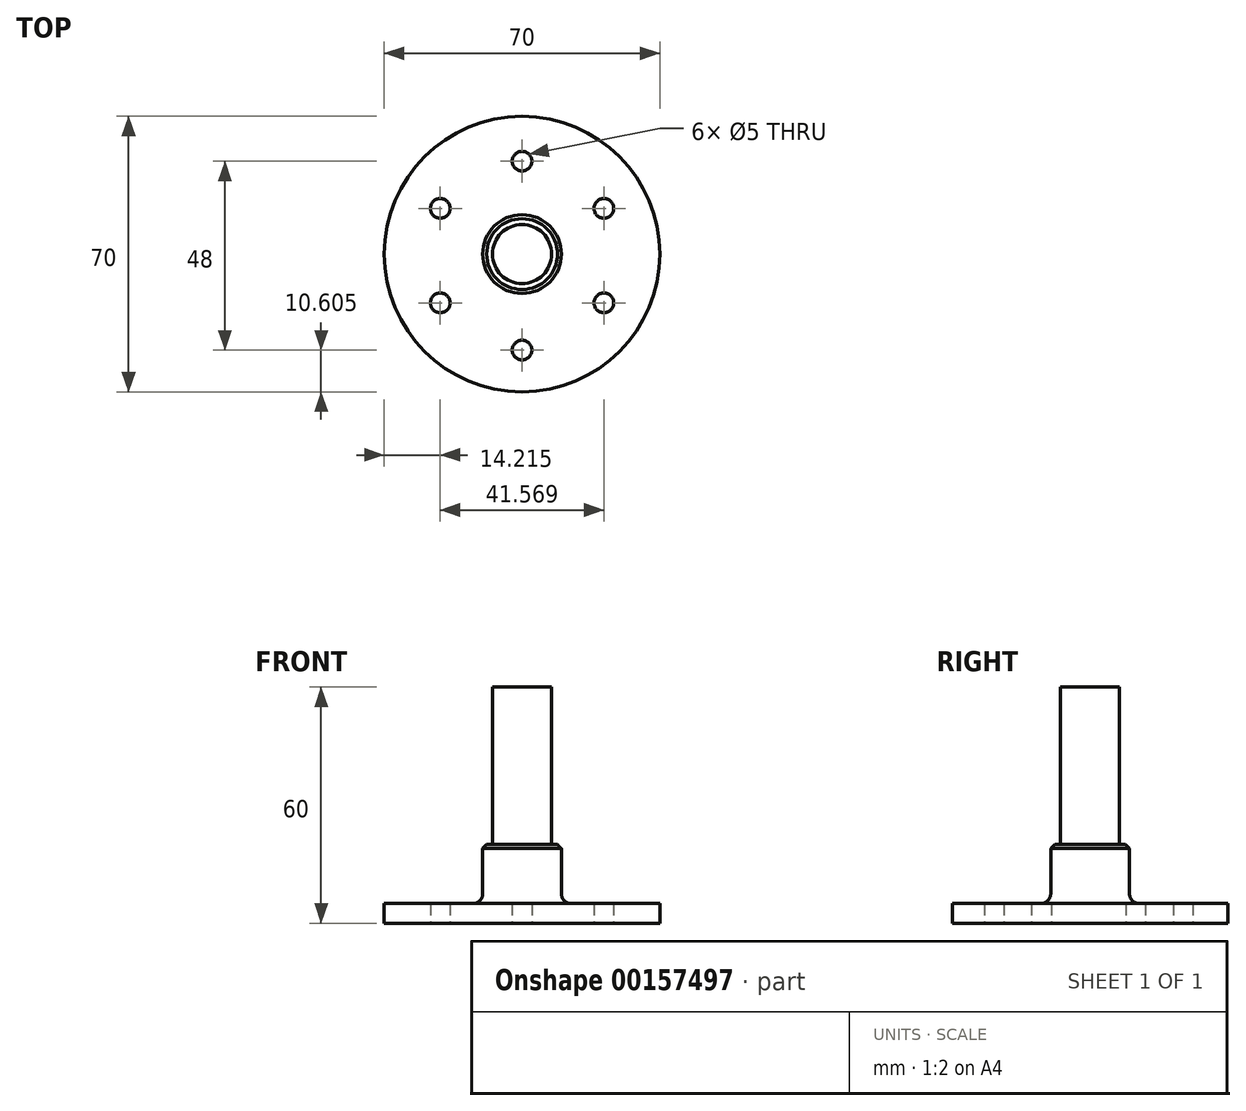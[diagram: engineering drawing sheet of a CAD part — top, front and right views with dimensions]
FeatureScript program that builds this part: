
annotation { "Feature Type Name" : "Feature", "Feature Type Description" : "" }
export const myFeature = defineFeature(function(context is Context, id is Id, definition is map)
    precondition{}
    {
        {
            var Q0;
            Q0=qCreatedBy(makeId("Top.planeOp"),FACE);
            var sketch = newSketch(context, id + "F0", { "sketchPlane" : qUnion([Q0])});
            skCircle(sketch, "E0", {"center": v(0, 0) * mm, "radius": 35 * mm});
            skCircle(sketch, "E1", {"center": v(0, 23.6) * mm, "radius": 2.5 * mm});
            skCircle(sketch, "E2.1.0", {"center": v(-20.78, 11.6) * mm, "radius": 2.5 * mm});
            skCircle(sketch, "E2.2.0", {"center": v(-20.78, -12.4) * mm, "radius": 2.5 * mm});
            skCircle(sketch, "E2.3.0", {"center": v(0, -24.4) * mm, "radius": 2.5 * mm});
            skCircle(sketch, "E2.4.0", {"center": v(20.78, -12.4) * mm, "radius": 2.5 * mm});
            skCircle(sketch, "E2.5.0", {"center": v(20.78, 11.6) * mm, "radius": 2.5 * mm});
            skPoint(sketch, "E2.center", {"position": v(0, -0.4) * mm});
            skSolve(sketch);
        }
        {
            var Q0;
            Q0=makeQuery(id+"F0.imprint","IMPRINT",FACE,{"disambiguationData":[TD([[makeQuery(id+"F0.imprint","IMPRINT",EDGE,{"derivedFrom":sQuery(id+"F0.wireOp",EDGE,"E0")}),1.0]])]});
            extrude(context, id + "F1", {"entities" : qUnion([Q0]), "depth" : 5 * mm});
        }
        {
            var Q0;
            Q0=qCreatedBy(makeId("Top.planeOp"),FACE);
            var sketch = newSketch(context, id + "F2", { "sketchPlane" : qUnion([Q0])});
            skCircle(sketch, "E3", {"center": v(0, 0) * mm, "radius": 10 * mm});
            skSolve(sketch);
        }
        {
            var Q0;
            Q0=makeQuery(id+"F2.imprint","IMPRINT",FACE,{"disambiguationData":[TD([[makeQuery(id+"F2.imprint","IMPRINT",EDGE,{"derivedFrom":sQuery(id+"F2.wireOp",EDGE,"E3")}),1.0]])]});
            extrude(context, id + "F3", {"entities" : qUnion([Q0]), "operationType" : NewBodyOperationType.ADD, "depth" : 20 * mm});
        }
        {
            var Q0;
            Q0=qCreatedBy(makeId("Top.planeOp"),FACE);
            var sketch = newSketch(context, id + "F4", { "sketchPlane" : qUnion([Q0])});
            skCircle(sketch, "E4", {"center": v(0, 0) * mm, "radius": 7.5 * mm});
            skSolve(sketch);
        }
        {
            var Q0;
            Q0 = qSketchRegion(id + "F4", true);
            extrude(context, id + "F5", {"entities" : qUnion([Q0]), "operationType" : NewBodyOperationType.ADD, "depth" : 60 * mm});
        }
        {
            var Q0;
            Q0=makeQuery(id+"F3.boolean.opBoolean","INTERSECT",EDGE,{"derivedFrom":[makeQuery(id+"F1.opExtrude","CAP_FACE",FACE,{"disambiguationData":[OSD([sQuery(id+"F0.wireOp",EDGE,"E0"),sQuery(id+"F0.wireOp",EDGE,"E1"),sQuery(id+"F0.wireOp",EDGE,"E2.1.0"),sQuery(id+"F0.wireOp",EDGE,"E2.2.0"),sQuery(id+"F0.wireOp",EDGE,"E2.3.0"),sQuery(id+"F0.wireOp",EDGE,"E2.4.0"),sQuery(id+"F0.wireOp",EDGE,"E2.5.0"),sQuery(id+"F0.wireOp",EDGE,"E2.6.0"),sQuery(id+"F0.wireOp",EDGE,"E2.7.0")])],"isStart":false}),makeQuery(id+"F3.opExtrude","SWEPT_FACE",FACE,{"disambiguationData":[OSD([sQuery(id+"F2.wireOp",EDGE,"E3")])]})]});
            fillet(context, id + "F6", {"entities" : qUnion([Q0]), "radius" : 2.5 * mm, "tangentPropagation" : true, "allowEdgeOverflow" : false});
        }
        {
            var Q0;
            Q0=makeQuery(id+"F3.opExtrude","CAP_EDGE",EDGE,{"disambiguationData":[OSD([sQuery(id+"F2.wireOp",EDGE,"E3")])],"isStart":false});
            chamfer(context, id + "F7", {"entities" : qUnion([Q0]), "width" : 1 * mm, "tangentPropagation" : true});
        }
    });
